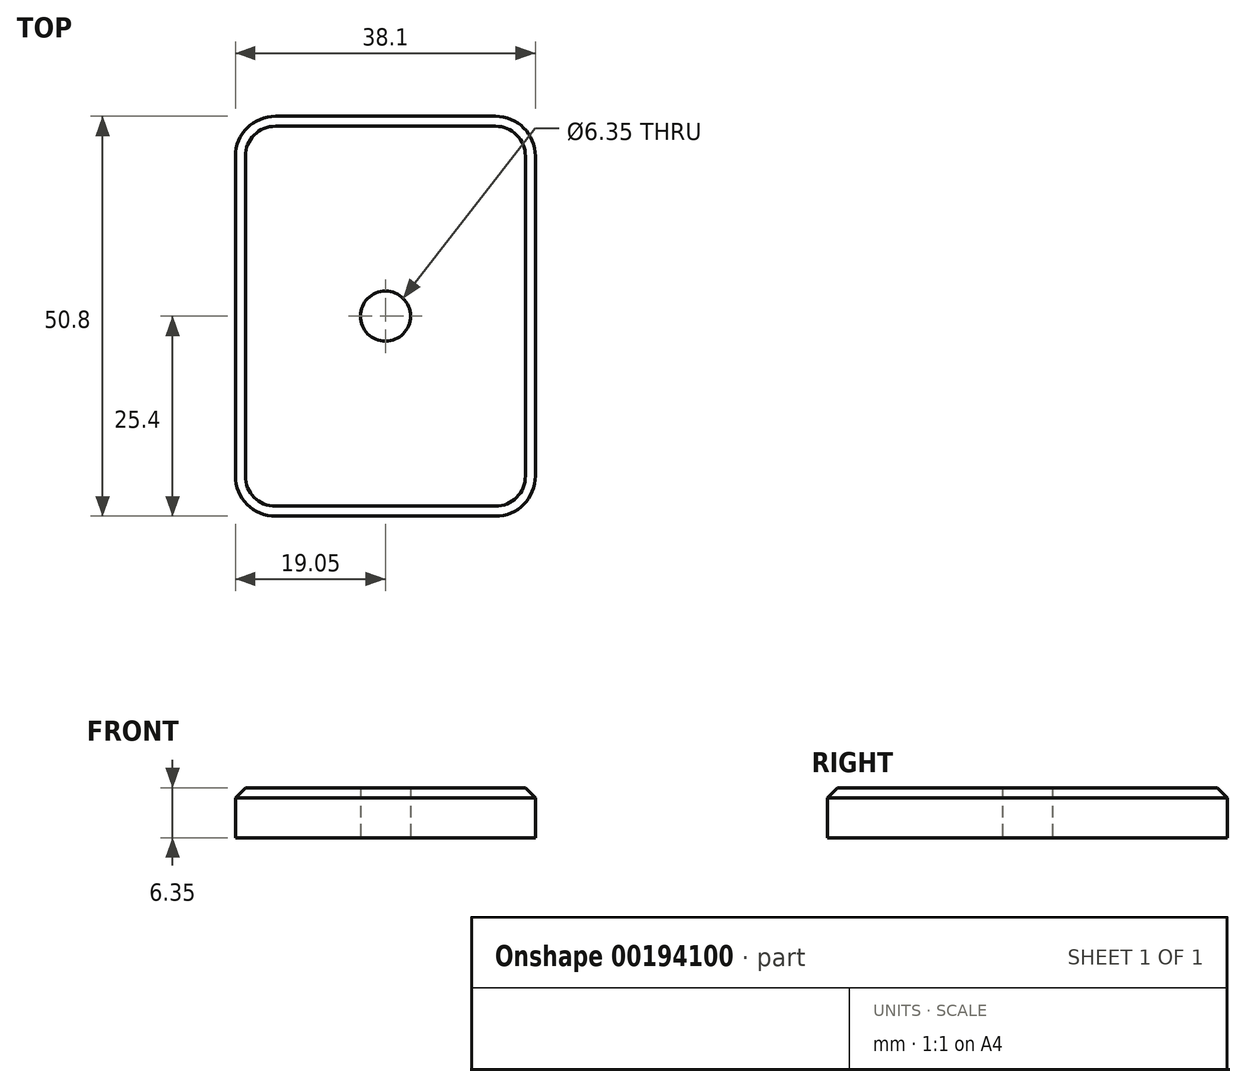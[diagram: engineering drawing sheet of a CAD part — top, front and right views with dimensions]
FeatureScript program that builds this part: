
annotation { "Feature Type Name" : "Feature", "Feature Type Description" : "" }
export const myFeature = defineFeature(function(context is Context, id is Id, definition is map)
    precondition{}
    {
        {
            var Q0;
            Q0=qCreatedBy(makeId("Top.planeOp"),FACE);
            var sketch = newSketch(context, id + "F0", { "sketchPlane" : qUnion([Q0])});
            skLineSegment(sketch, "E0.bottom", {"start": v(0, 0) * mm, "end": v(38.1, 0) * mm});
            skLineSegment(sketch, "E0.top", {"start": v(0, 50.8) * mm, "end": v(38.1, 50.8) * mm});
            skLineSegment(sketch, "E0.left", {"start": v(0, 0) * mm, "end": v(0, 50.8) * mm});
            skLineSegment(sketch, "E0.right", {"start": v(38.1, 0) * mm, "end": v(38.1, 50.8) * mm});
            skCircle(sketch, "E1", {"center": v(19.05, 25.4) * mm, "radius": 3.18 * mm});
            skPoint(sketch, "E1.centerSnap0", {"position": v(38.1, 25.4) * mm});
            skPoint(sketch, "E1.centerSnap1", {"position": v(19.05, 50.8) * mm});
            skSolve(sketch);
        }
        {
            var Q0;
            Q0=makeQuery(id+"F0.imprint","IMPRINT",FACE,{"disambiguationData":[TD([[makeQuery(id+"F0.imprint","IMPRINT",EDGE,{"derivedFrom":sQuery(id+"F0.wireOp",EDGE,"E0.bottom")}),1.0]])]});
            extrude(context, id + "F1", {"entities" : qUnion([Q0]), "offsetDistance" : 25.4 * mm, "depth" : 6.35 * mm});
        }
        {
            var Q0;
            Q0=makeQuery(id+"F1.opExtrude","SWEPT_EDGE",EDGE,{"disambiguationData":[OSD([sQuery(id+"F0.wireOp",EDGE,"E0.top"),sQuery(id+"F0.wireOp",EDGE,"E0.left")])]});
            var Q1;
            Q1=makeQuery(id+"F1.opExtrude","SWEPT_EDGE",EDGE,{"disambiguationData":[OSD([sQuery(id+"F0.wireOp",EDGE,"E0.bottom"),sQuery(id+"F0.wireOp",EDGE,"E0.left")])]});
            var Q2;
            Q2=makeQuery(id+"F1.opExtrude","SWEPT_EDGE",EDGE,{"disambiguationData":[OSD([sQuery(id+"F0.wireOp",EDGE,"E0.bottom"),sQuery(id+"F0.wireOp",EDGE,"E0.right")])]});
            var Q3;
            Q3=makeQuery(id+"F1.opExtrude","SWEPT_EDGE",EDGE,{"disambiguationData":[OSD([sQuery(id+"F0.wireOp",EDGE,"E0.top"),sQuery(id+"F0.wireOp",EDGE,"E0.right")])]});
            fillet(context, id + "F2", {"entities" : qUnion([Q0, Q1, Q2, Q3]), "radius" : 5.08 * mm, "tangentPropagation" : true, "allowEdgeOverflow" : false});
        }
        {
            var Q0;
            Q0=makeQuery(id+"F1.opExtrude","CAP_EDGE",EDGE,{"disambiguationData":[OSD([sQuery(id+"F0.wireOp",EDGE,"E0.top")])],"isStart":false});
            chamfer(context, id + "F3", {"entities" : qUnion([Q0]), "width" : 1.27 * mm, "tangentPropagation" : true});
        }
    });
